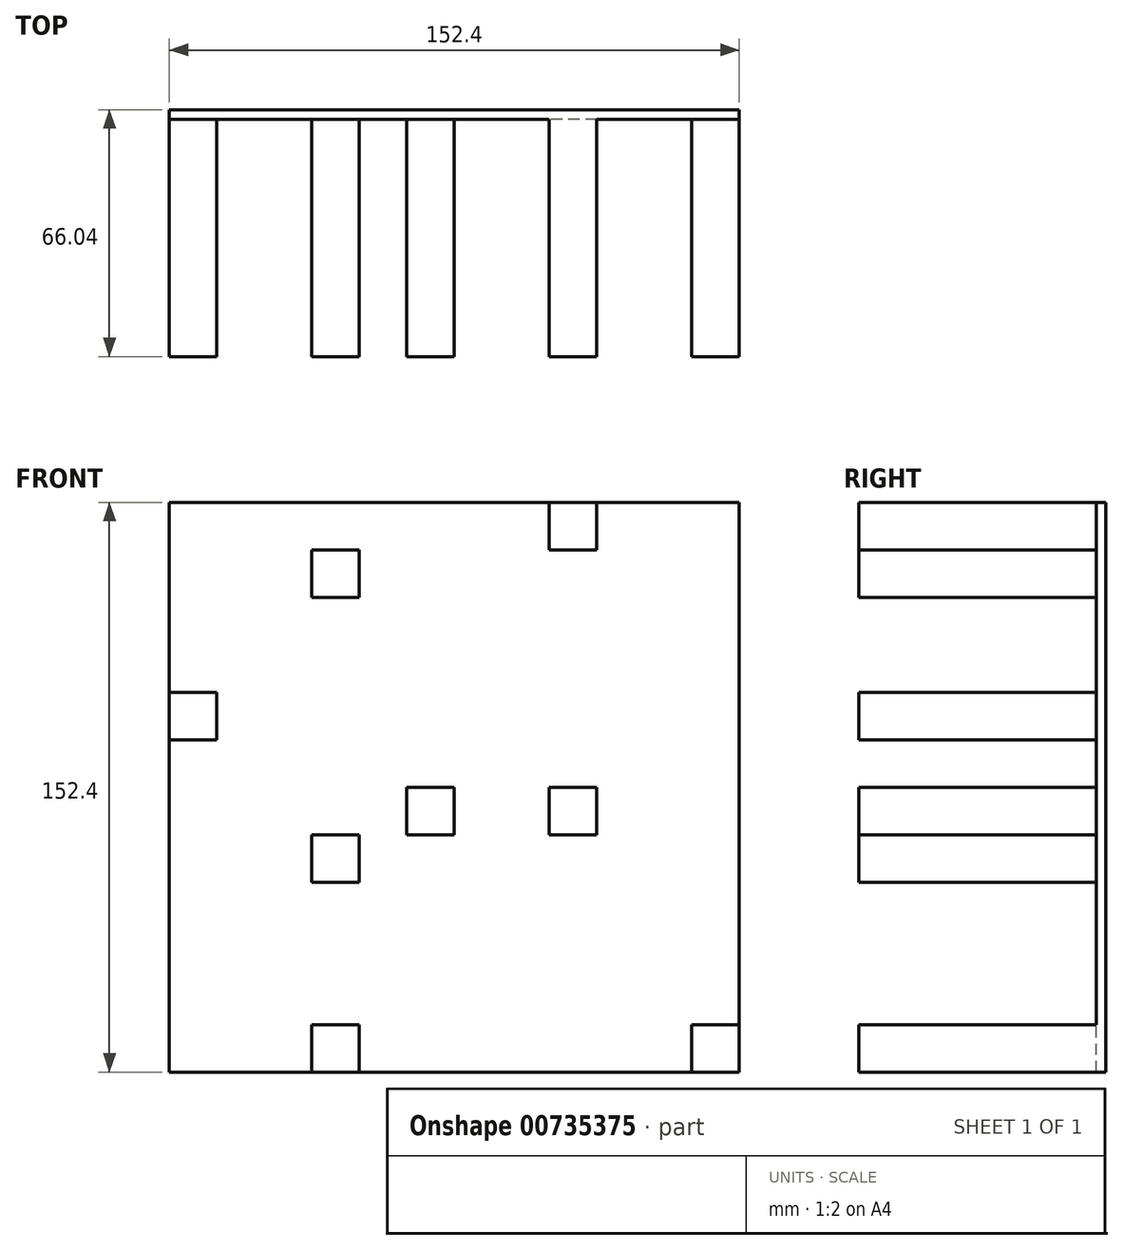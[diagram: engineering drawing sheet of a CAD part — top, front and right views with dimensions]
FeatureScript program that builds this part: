
annotation { "Feature Type Name" : "Feature", "Feature Type Description" : "" }
export const myFeature = defineFeature(function(context is Context, id is Id, definition is map)
    precondition{}
    {
        {
            var Q0;
            Q0=qCreatedBy(makeId("Front.planeOp"),FACE);
            var sketch = newSketch(context, id + "F0", { "sketchPlane" : qUnion([Q0])});
            skLineSegment(sketch, "E0.bottom", {"start": v(0, 0) * mm, "end": v(-152.4, 0) * mm});
            skLineSegment(sketch, "E0.top", {"start": v(0, 152.4) * mm, "end": v(-152.4, 152.4) * mm});
            skLineSegment(sketch, "E0.left", {"start": v(0, 0) * mm, "end": v(0, 152.4) * mm});
            skLineSegment(sketch, "E0.right", {"start": v(-152.4, 0) * mm, "end": v(-152.4, 152.4) * mm});
            skSolve(sketch);
        }
        {
            var Q0;
            Q0 = qSketchRegion(id + "F0", true);
            extrude(context, id + "F1", {"entities" : qUnion([Q0]), "depth" : 152.4 * mm, "offsetDistance" : 25.4 * mm});
        }
        {
            var Q0;
            Q0=makeQuery(id+"F1.opExtrude","CAP_FACE",FACE,{"disambiguationData":[OSD([sQuery(id+"F0.wireOp",EDGE,"E0.bottom"),sQuery(id+"F0.wireOp",EDGE,"E0.top"),sQuery(id+"F0.wireOp",EDGE,"E0.left"),sQuery(id+"F0.wireOp",EDGE,"E0.right")])],"isStart":false});
            var sketch = newSketch(context, id + "F2", { "sketchPlane" : qUnion([Q0])});
            skLineSegment(sketch, "E1.bottom", {"start": v(0, 0) * mm, "end": v(-12.7, 0) * mm});
            skLineSegment(sketch, "E1.top", {"start": v(0, 12.7) * mm, "end": v(-12.7, 12.7) * mm});
            skLineSegment(sketch, "E1.left", {"start": v(0, 0) * mm, "end": v(0, 12.7) * mm});
            skLineSegment(sketch, "E1.right", {"start": v(-12.7, 0) * mm, "end": v(-12.7, 12.7) * mm});
            skLineSegment(sketch, "E2.bottom", {"start": v(-101.6, 0) * mm, "end": v(-114.3, 0) * mm});
            skLineSegment(sketch, "E2.top", {"start": v(-101.6, 12.7) * mm, "end": v(-114.3, 12.7) * mm});
            skLineSegment(sketch, "E2.left", {"start": v(-101.6, 0) * mm, "end": v(-101.6, 12.7) * mm});
            skLineSegment(sketch, "E2.right", {"start": v(-114.3, 0) * mm, "end": v(-114.3, 12.7) * mm});
            skLineSegment(sketch, "E3.bottom", {"start": v(-101.6, 127) * mm, "end": v(-114.3, 127) * mm});
            skLineSegment(sketch, "E3.top", {"start": v(-101.6, 139.7) * mm, "end": v(-114.3, 139.7) * mm});
            skLineSegment(sketch, "E3.left", {"start": v(-101.6, 127) * mm, "end": v(-101.6, 139.7) * mm});
            skLineSegment(sketch, "E3.right", {"start": v(-114.3, 127) * mm, "end": v(-114.3, 139.7) * mm});
            skLineSegment(sketch, "E4.bottom", {"start": v(-38.1, 63.5) * mm, "end": v(-50.8, 63.5) * mm});
            skLineSegment(sketch, "E4.top", {"start": v(-38.1, 76.2) * mm, "end": v(-50.8, 76.2) * mm});
            skLineSegment(sketch, "E4.left", {"start": v(-38.1, 63.5) * mm, "end": v(-38.1, 76.2) * mm});
            skLineSegment(sketch, "E4.right", {"start": v(-50.8, 63.5) * mm, "end": v(-50.8, 76.2) * mm});
            skLineSegment(sketch, "E5.bottom", {"start": v(-114.3, 63.5) * mm, "end": v(-101.6, 63.5) * mm});
            skLineSegment(sketch, "E5.top", {"start": v(-114.3, 50.8) * mm, "end": v(-101.6, 50.8) * mm});
            skLineSegment(sketch, "E5.left", {"start": v(-114.3, 63.5) * mm, "end": v(-114.3, 50.8) * mm});
            skLineSegment(sketch, "E5.right", {"start": v(-101.6, 63.5) * mm, "end": v(-101.6, 50.8) * mm});
            skLineSegment(sketch, "E6.bottom", {"start": v(-38.1, 152.4) * mm, "end": v(-50.8, 152.4) * mm});
            skLineSegment(sketch, "E6.top", {"start": v(-38.1, 139.7) * mm, "end": v(-50.8, 139.7) * mm});
            skLineSegment(sketch, "E6.left", {"start": v(-38.1, 152.4) * mm, "end": v(-38.1, 139.7) * mm});
            skLineSegment(sketch, "E6.right", {"start": v(-50.8, 152.4) * mm, "end": v(-50.8, 139.7) * mm});
            skLineSegment(sketch, "E7.bottom", {"start": v(-152.4, 101.6) * mm, "end": v(-139.7, 101.6) * mm});
            skLineSegment(sketch, "E7.top", {"start": v(-152.4, 88.9) * mm, "end": v(-139.7, 88.9) * mm});
            skLineSegment(sketch, "E7.left", {"start": v(-152.4, 101.6) * mm, "end": v(-152.4, 88.9) * mm});
            skLineSegment(sketch, "E7.right", {"start": v(-139.7, 101.6) * mm, "end": v(-139.7, 88.9) * mm});
            skLineSegment(sketch, "E8.bottom", {"start": v(-76.2, 76.2) * mm, "end": v(-88.9, 76.2) * mm});
            skLineSegment(sketch, "E8.top", {"start": v(-76.2, 63.5) * mm, "end": v(-88.9, 63.5) * mm});
            skLineSegment(sketch, "E8.left", {"start": v(-76.2, 76.2) * mm, "end": v(-76.2, 63.5) * mm});
            skLineSegment(sketch, "E8.right", {"start": v(-88.9, 76.2) * mm, "end": v(-88.9, 63.5) * mm});
            skSolve(sketch);
        }
        {
            var Q0;
            Q0 = qSketchRegion(id + "F2", true);
            extrude(context, id + "F3", {"entities" : qUnion([Q0]), "operationType" : NewBodyOperationType.ADD, "oppositeDirection" : true, "depth" : -63.5 * mm, "offsetDistance" : 25.4 * mm});
        }
        {
            var Q0;
            Q0 = qSketchRegion(id + "F0", true);
            extrude(context, id + "F4", {"entities" : qUnion([Q0]), "operationType" : NewBodyOperationType.REMOVE, "oppositeDirection" : true, "depth" : -149.86 * mm, "offsetDistance" : 25.4 * mm});
        }
    });
